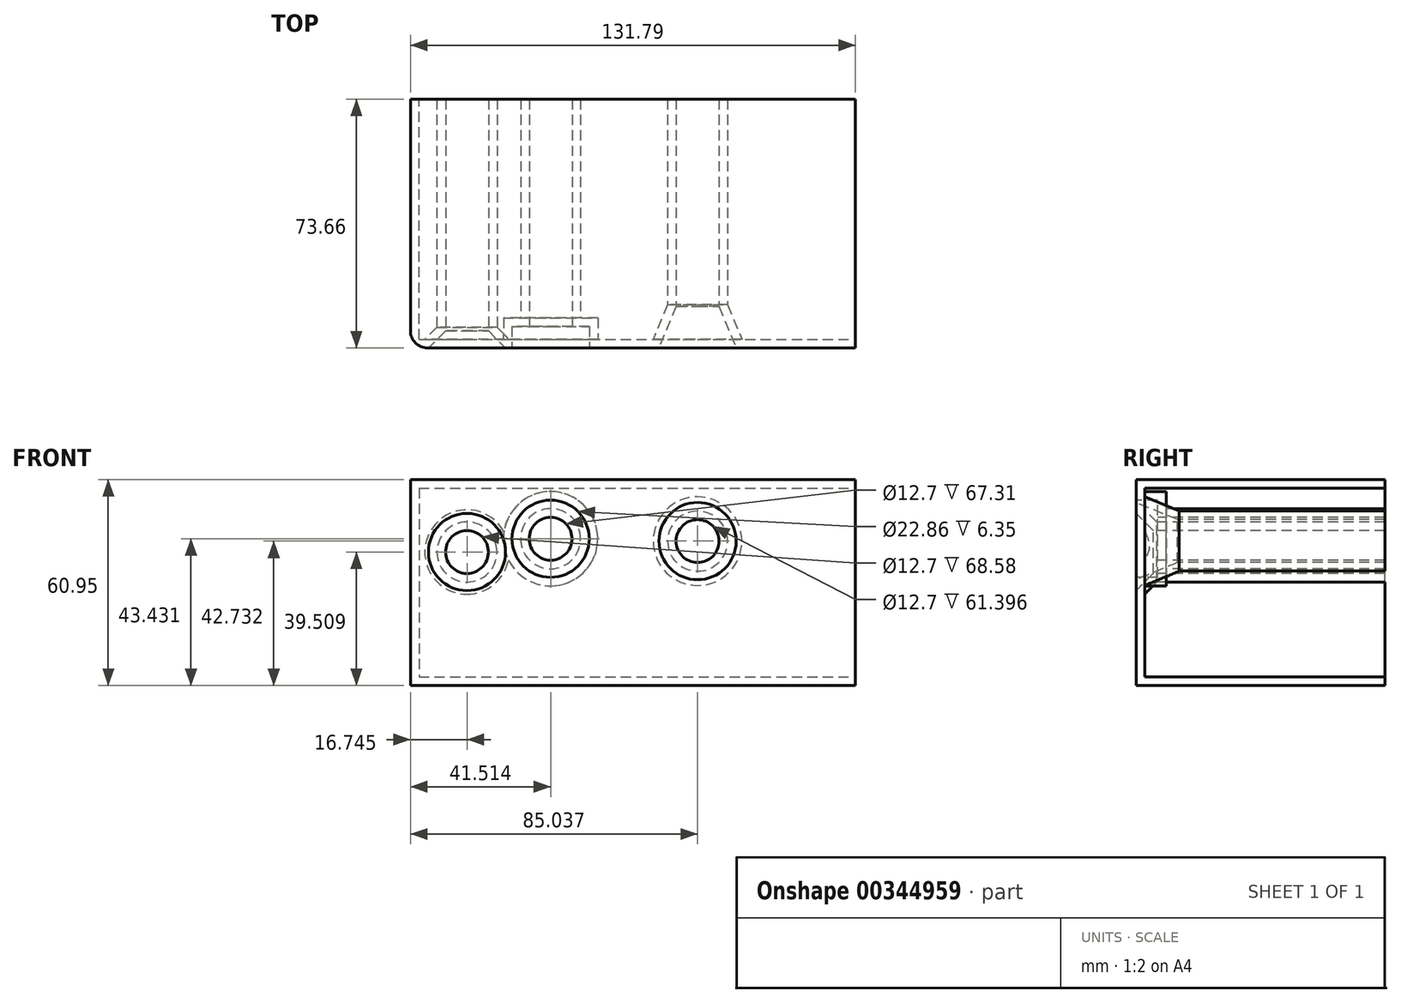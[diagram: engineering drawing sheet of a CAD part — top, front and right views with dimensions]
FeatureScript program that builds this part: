
annotation { "Feature Type Name" : "Feature", "Feature Type Description" : "" }
export const myFeature = defineFeature(function(context is Context, id is Id, definition is map)
    precondition{}
    {
        {
            var Q0;
            Q0=qCreatedBy(makeId("Front.planeOp"),FACE);
            var sketch = newSketch(context, id + "F0", { "sketchPlane" : qUnion([Q0])});
            skLineSegment(sketch, "E0.bottom", {"start": v(-62.21, 27.5) * mm, "end": v(69.58, 27.5) * mm});
            skLineSegment(sketch, "E0.top", {"start": v(-62.21, -33.44) * mm, "end": v(69.58, -33.44) * mm});
            skLineSegment(sketch, "E0.left", {"start": v(-62.21, 27.5) * mm, "end": v(-62.21, -33.44) * mm});
            skLineSegment(sketch, "E0.right", {"start": v(69.58, 27.5) * mm, "end": v(69.58, -33.44) * mm});
            skSolve(sketch);
        }
        {
            var Q0;
            Q0=makeQuery(id+"F0.imprint","IMPRINT",FACE,{"disambiguationData":[TD([[makeQuery(id+"F0.imprint","IMPRINT",EDGE,{"derivedFrom":sQuery(id+"F0.wireOp",EDGE,"E0.bottom")}),-1.0]])]});
            extrude(context, id + "F1", {"entities" : qUnion([Q0]), "endBound" : BoundingType.SYMMETRIC, "depth" : 73.66 * mm});
        }
        {
            var Q0;
            Q0=makeQuery(id+"F1.opExtrude","CAP_FACE",FACE,{"disambiguationData":[OSD([sQuery(id+"F0.wireOp",EDGE,"E0.bottom"),sQuery(id+"F0.wireOp",EDGE,"E0.top"),sQuery(id+"F0.wireOp",EDGE,"E0.left"),sQuery(id+"F0.wireOp",EDGE,"E0.right")])],"isStart":false});
            var sketch = newSketch(context, id + "F2", { "sketchPlane" : qUnion([Q0])});
            skCircle(sketch, "E1", {"center": v(-45.99, 11.15) * mm, "radius": 4.49 * mm});
            skPoint(sketch, "E2", {"position": v(-20.7, 10) * mm});
            skSolve(sketch);
        }
        {
            var Q0;
            Q0=sQuery(id+"F2.wireOp",VERTEX,"E2");
            var Q1;
            Q1=makeQuery(id+"F1.opExtrude","SWEPT_BODY",BODY,{"disambiguationData":[OSD([sQuery(id+"F0.wireOp",EDGE,"E0.bottom"),sQuery(id+"F0.wireOp",EDGE,"E0.top"),sQuery(id+"F0.wireOp",EDGE,"E0.left"),sQuery(id+"F0.wireOp",EDGE,"E0.right")])]});
            hole(context, id + "F3", {"style" : HoleStyle.C_BORE, "endStyle" : HoleEndStyle.THROUGH, "holeDiameter" : 12.7 * mm, "cBoreDiameter" : 22.86 * mm, "cBoreDepth" : 6.35 * mm, "isTappedThrough" : true, "tappedDepth" : 12.7 * mm, "tapClearance" : 3, "locations" : qUnion([Q0]), "scope" : qUnion([Q1])});
        }
        {
            var Q0;
            Q0=makeQuery(id+"F1.opExtrude","CAP_FACE",FACE,{"disambiguationData":[OSD([sQuery(id+"F0.wireOp",EDGE,"E0.bottom"),sQuery(id+"F0.wireOp",EDGE,"E0.top"),sQuery(id+"F0.wireOp",EDGE,"E0.left"),sQuery(id+"F0.wireOp",EDGE,"E0.right")])],"isStart":false});
            var sketch = newSketch(context, id + "F4", { "sketchPlane" : qUnion([Q0])});
            skPoint(sketch, "E3", {"position": v(-45.46, 6.07) * mm});
            skSolve(sketch);
        }
        {
            var Q0;
            Q0=sQuery(id+"F4.wireOp",VERTEX,"E3");
            var Q1;
            Q1=makeQuery(id+"F1.opExtrude","SWEPT_BODY",BODY,{"disambiguationData":[OSD([sQuery(id+"F0.wireOp",EDGE,"E0.bottom"),sQuery(id+"F0.wireOp",EDGE,"E0.top"),sQuery(id+"F0.wireOp",EDGE,"E0.left"),sQuery(id+"F0.wireOp",EDGE,"E0.right")])]});
            hole(context, id + "F5", {"style" : HoleStyle.C_SINK, "endStyle" : HoleEndStyle.THROUGH, "holeDiameter" : 12.7 * mm, "cSinkDiameter" : 22.86 * mm, "cSinkAngle" : 90 * degree, "isTappedThrough" : true, "tappedDepth" : 12.7 * mm, "tapClearance" : 3, "locations" : qUnion([Q0]), "scope" : qUnion([Q1])});
        }
        {
            var Q0;
            Q0=makeQuery(id+"F1.opExtrude","CAP_FACE",FACE,{"disambiguationData":[OSD([sQuery(id+"F0.wireOp",EDGE,"E0.bottom"),sQuery(id+"F0.wireOp",EDGE,"E0.top"),sQuery(id+"F0.wireOp",EDGE,"E0.left"),sQuery(id+"F0.wireOp",EDGE,"E0.right")])],"isStart":false});
            var sketch = newSketch(context, id + "F6", { "sketchPlane" : qUnion([Q0])});
            skPoint(sketch, "E4", {"position": v(22.83, 9.3) * mm});
            skSolve(sketch);
        }
        {
            var Q0;
            Q0=sQuery(id+"F6.wireOp",VERTEX,"E4");
            var Q1;
            Q1=makeQuery(id+"F1.opExtrude","SWEPT_BODY",BODY,{"disambiguationData":[OSD([sQuery(id+"F0.wireOp",EDGE,"E0.bottom"),sQuery(id+"F0.wireOp",EDGE,"E0.top"),sQuery(id+"F0.wireOp",EDGE,"E0.left"),sQuery(id+"F0.wireOp",EDGE,"E0.right")])]});
            hole(context, id + "F7", {"style" : HoleStyle.C_SINK, "endStyle" : HoleEndStyle.THROUGH, "holeDiameter" : 12.7 * mm, "cSinkDiameter" : 22.86 * mm, "cSinkAngle" : 45 * degree, "isTappedThrough" : true, "tappedDepth" : 12.7 * mm, "tapClearance" : 3, "locations" : qUnion([Q0]), "scope" : qUnion([Q1])});
        }
        {
            var Q0;
            Q0=makeQuery(id+"F1.opExtrude","SWEPT_FACE",FACE,{"disambiguationData":[OSD([sQuery(id+"F0.wireOp",EDGE,"E0.right")])]});
            var Q1;
            Q1=makeQuery(id+"F1.opExtrude","CAP_FACE",FACE,{"disambiguationData":[OSD([sQuery(id+"F0.wireOp",EDGE,"E0.bottom"),sQuery(id+"F0.wireOp",EDGE,"E0.top"),sQuery(id+"F0.wireOp",EDGE,"E0.left"),sQuery(id+"F0.wireOp",EDGE,"E0.right")])],"isStart":true});
            shell(context, id + "F8", {"entities" : qUnion([Q0, Q1]), "thickness" : 2.54 * mm});
        }
        {
            var Q0;
            {var subQ0=sQuery(id+"F0.wireOp",EDGE,"E0.right");var subQ1=sQuery(id+"F0.wireOp",EDGE,"E0.left");var subQ2=sQuery(id+"F0.wireOp",EDGE,"E0.top");var subQ3=sQuery(id+"F0.wireOp",EDGE,"E0.bottom");Q0=makeQuery(id+"F8.opShell","OFFSET_FACE",FACE,{"disambiguationData":[OSD([subQ3,subQ2,subQ1,subQ0]),TDD([makeQuery(id+"F1.opExtrude","CAP_FACE",FACE,{"disambiguationData":[OSD([subQ3,subQ2,subQ1,subQ0])],"isStart":false})])]});}
            var sketch = newSketch(context, id + "F9", { "sketchPlane" : qUnion([Q0])});
            skSolve(sketch);
        }
        {
            var Q0;
            Q0=makeQuery(id+"F1.opExtrude","CAP_EDGE",EDGE,{"disambiguationData":[OSD([sQuery(id+"F0.wireOp",EDGE,"E0.left")])],"isStart":false});
            fillet(context, id + "F10", {"entities" : qUnion([Q0]), "radius" : 5.08 * mm, "tangentPropagation" : true, "allowEdgeOverflow" : false});
        }
    });
